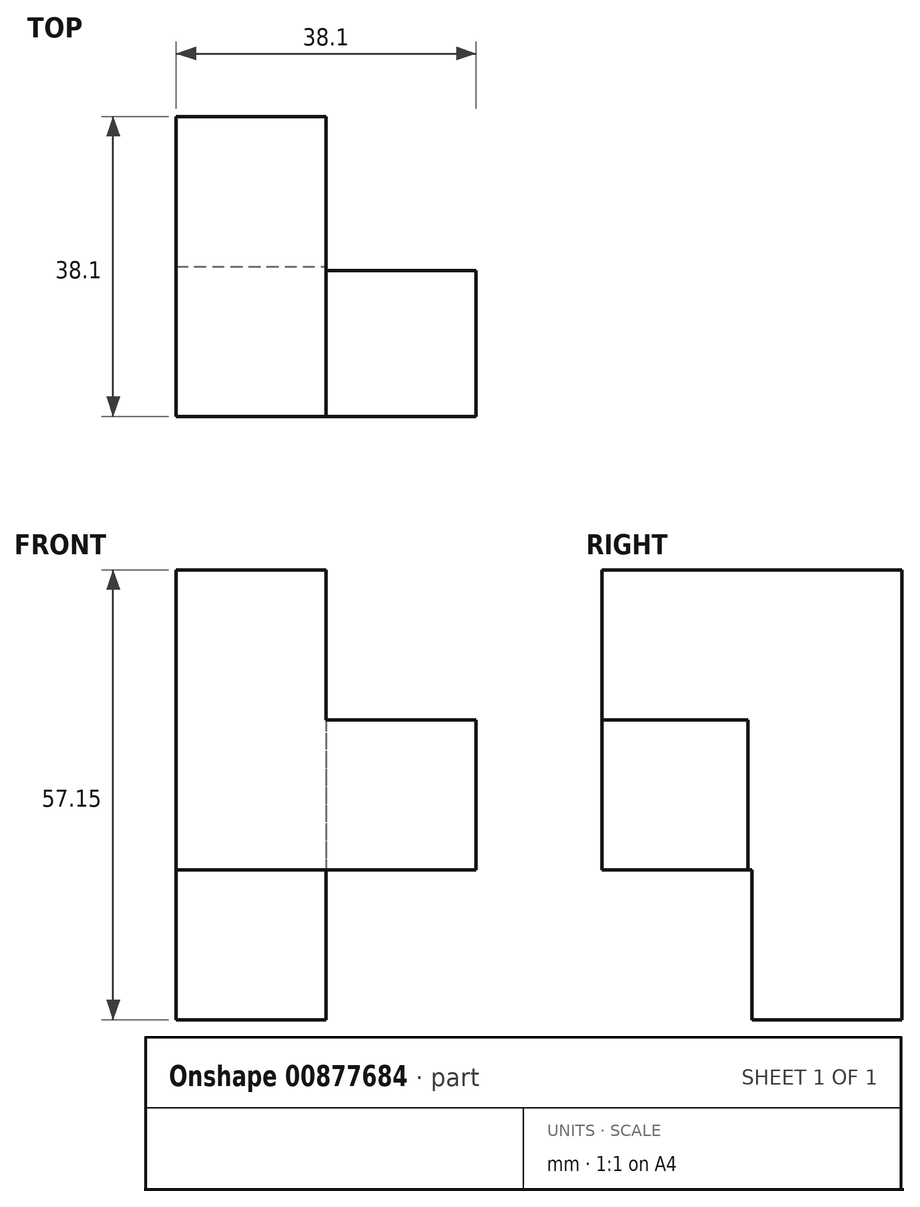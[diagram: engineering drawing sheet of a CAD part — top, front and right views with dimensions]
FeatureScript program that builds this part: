
annotation { "Feature Type Name" : "Feature", "Feature Type Description" : "" }
export const myFeature = defineFeature(function(context is Context, id is Id, definition is map)
    precondition{}
    {
        {
            var Q0;
            Q0=qCreatedBy(makeId("Top.planeOp"),FACE);
            var sketch = newSketch(context, id + "F0", { "sketchPlane" : qUnion([Q0])});
            skLineSegment(sketch, "E0.bottom", {"start": v(0, 0) * mm, "end": v(19.05, 0) * mm});
            skLineSegment(sketch, "E0.top", {"start": v(0, -19.05) * mm, "end": v(19.05, -19.05) * mm});
            skLineSegment(sketch, "E0.left", {"start": v(0, 0) * mm, "end": v(0, -19.05) * mm});
            skLineSegment(sketch, "E0.right", {"start": v(19.05, 0) * mm, "end": v(19.05, -19.05) * mm});
            skSolve(sketch);
        }
        {
            var Q0;
            Q0=qSketchRegion(id+"F0",true);
            var Q1;
            Q1=qSketchRegion(id+"F2",true);
            extrude(context, id + "F1", {"entities" : qUnion([Q0, Q1]), "depth" : 57.15 * mm});
        }
        {
            var Q0;
            Q0=makeQuery(id+"F1.opExtrude","SWEPT_FACE",FACE,{"disambiguationData":[OSD([sQuery(id+"F0.wireOp",EDGE,"E0.top")])]});
            var sketch = newSketch(context, id + "F2", { "sketchPlane" : qUnion([Q0])});
            skLineSegment(sketch, "E1.bottom", {"start": v(0, 57.15) * mm, "end": v(19.05, 57.15) * mm});
            skLineSegment(sketch, "E1.top", {"start": v(0, 19.05) * mm, "end": v(19.05, 19.05) * mm});
            skLineSegment(sketch, "E1.left", {"start": v(0, 57.15) * mm, "end": v(0, 19.05) * mm});
            skLineSegment(sketch, "E1.right", {"start": v(19.05, 57.15) * mm, "end": v(19.05, 19.05) * mm});
            skSolve(sketch);
        }
        {
            var Q0;
            Q0=qSketchRegion(id+"F2",true);
            extrude(context, id + "F3", {"entities" : qUnion([Q0]), "operationType" : NewBodyOperationType.ADD, "depth" : 19.05 * mm});
        }
        {
            var Q0;
            Q0=makeQuery(id+"F3.boolean.opBoolean","MERGE",FACE,{"derivedFrom":[makeQuery(id+"F1.opExtrude","SWEPT_FACE",FACE,{"disambiguationData":[OSD([sQuery(id+"F0.wireOp",EDGE,"E0.right")])]}),makeQuery(id+"F3.opExtrude","SWEPT_FACE",FACE,{"disambiguationData":[OSD([sQuery(id+"F2.wireOp",EDGE,"E1.right")])]})]});
            var sketch = newSketch(context, id + "F4", { "sketchPlane" : qUnion([Q0])});
            skLineSegment(sketch, "E2.left", {"start": v(-38.1, 19.05) * mm, "end": v(-38.1, 38.1) * mm});
            skLineSegment(sketch, "E3", {"start": v(-19.56, 38.1) * mm, "end": v(-19.56, 19.05) * mm});
            skLineSegment(sketch, "E4", {"start": v(-19.56, 38.1) * mm, "end": v(-38.1, 38.1) * mm});
            skLineSegment(sketch, "E5", {"start": v(-19.56, 19.05) * mm, "end": v(-38.1, 19.05) * mm});
            skSolve(sketch);
        }
        {
            var Q0;
            Q0=qSketchRegion(id+"F4",true);
            extrude(context, id + "F5", {"entities" : qUnion([Q0]), "operationType" : NewBodyOperationType.ADD, "depth" : 19.05 * mm});
        }
    });
